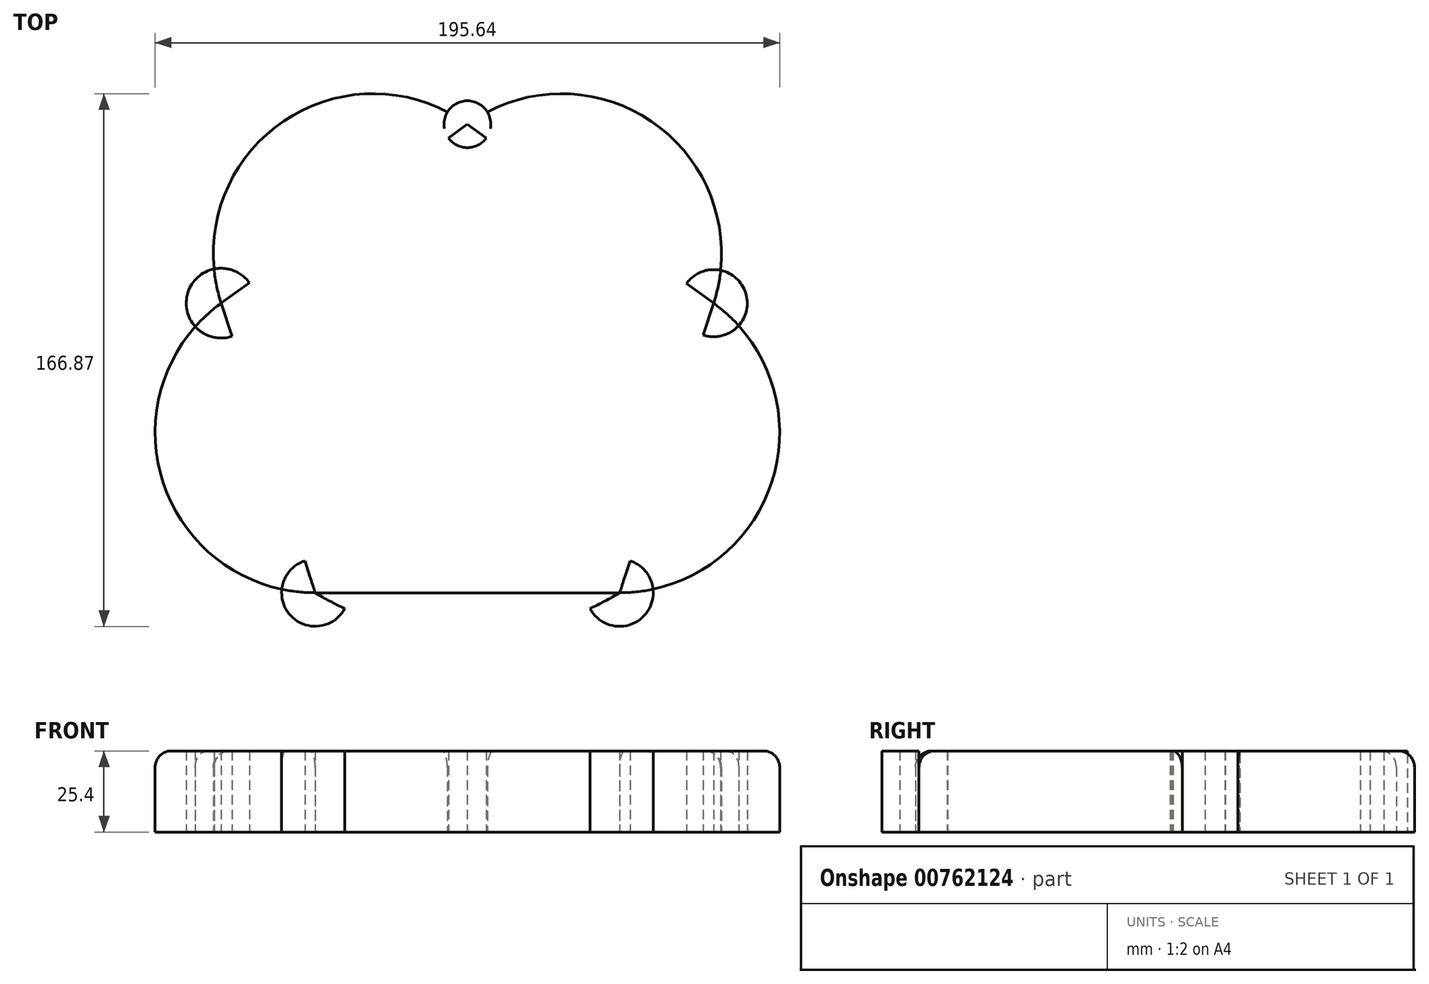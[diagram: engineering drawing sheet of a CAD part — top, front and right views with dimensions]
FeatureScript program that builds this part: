
annotation { "Feature Type Name" : "Feature", "Feature Type Description" : "" }
export const myFeature = defineFeature(function(context is Context, id is Id, definition is map)
    precondition{}
    {
        {
            var Q0;
            Q0=qCreatedBy(makeId("Top.planeOp"),FACE);
            var sketch = newSketch(context, id + "F0", { "sketchPlane" : qUnion([Q0])});
            skCircle(sketch, "E0.cCircle", {"center": v(0, 0) * mm, "radius": 65.63 * mm, "construction": true});
            skLineSegment(sketch, "E0.0", {"start": v(47.68, -65.63) * mm, "end": v(-47.68, -65.63) * mm});
            skLineSegment(sketch, "E0.1", {"start": v(-47.68, -65.63) * mm, "end": v(-77.15, 25.07) * mm});
            skLineSegment(sketch, "E0.2", {"start": v(-77.15, 25.07) * mm, "end": v(0, 81.12) * mm});
            skLineSegment(sketch, "E0.3", {"start": v(0, 81.12) * mm, "end": v(77.15, 25.07) * mm});
            skLineSegment(sketch, "E0.4", {"start": v(77.15, 25.07) * mm, "end": v(47.68, -65.63) * mm});
            skPoint(sketch, "E0.0.midPoint", {"position": v(0, -65.63) * mm});
            skCircle(sketch, "E1", {"center": v(-77.15, 25.07) * mm, "radius": 10.93 * mm});
            skCircle(sketch, "E2", {"center": v(0, 81.12) * mm, "radius": 7.34 * mm});
            skCircle(sketch, "E3", {"center": v(77.15, 25.07) * mm, "radius": 10.52 * mm});
            skCircle(sketch, "E4", {"center": v(47.68, -65.63) * mm, "radius": 10.54 * mm});
            skCircle(sketch, "E5", {"center": v(-47.68, -65.63) * mm, "radius": 10.5 * mm});
            skArc(sketch, "E6", {"start": v(-77.15, 25.07) * mm, "mid": v(-95.37, -30.99) * mm, "end": v(-47.68, -65.63) * mm});
            skArc(sketch, "E7", {"start": v(0, 81.12) * mm, "mid": v(-58.94, 81.12) * mm, "end": v(-77.15, 25.07) * mm});
            skArc(sketch, "E8", {"start": v(77.15, 25.07) * mm, "mid": v(58.94, 81.12) * mm, "end": v(0, 81.12) * mm});
            skArc(sketch, "E9", {"start": v(47.68, -65.63) * mm, "mid": v(95.37, -30.99) * mm, "end": v(77.15, 25.07) * mm});
            skArc(sketch, "E10", {"start": v(-47.68, -65.63) * mm, "mid": v(0, -79.02) * mm, "end": v(47.68, -65.63) * mm});
            skSolve(sketch);
        }
        {
            var Q0;
            {var subQ0=sQuery(id+"F0.wireOp",EDGE,"E7");var subQ1=sQuery(id+"F0.wireOp",EDGE,"E2");var subQ2=makeQuery(id+"F0.imprint","INTERSECT",VERTEX,{"derivedFrom":[subQ1,subQ0]});Q0=makeQuery(id+"F0.imprint","IMPRINT",FACE,{"disambiguationData":[TD([[makeQuery(id+"F0.imprint","IMPRINT",EDGE,{"disambiguationData":[TD([[subQ2,1.0]])],"derivedFrom":subQ1}),1.0]])]});}
            var Q1;
            {var subQ0=sQuery(id+"F0.wireOp",EDGE,"E8");var subQ1=sQuery(id+"F0.wireOp",EDGE,"E3");var subQ2=makeQuery(id+"F0.imprint","INTERSECT",VERTEX,{"derivedFrom":[subQ1,subQ0]});Q1=makeQuery(id+"F0.imprint","IMPRINT",FACE,{"disambiguationData":[TD([[makeQuery(id+"F0.imprint","IMPRINT",EDGE,{"disambiguationData":[TD([[subQ2,1.0]])],"derivedFrom":subQ1}),1.0]])]});}
            var Q2;
            {var subQ0=sQuery(id+"F0.wireOp",EDGE,"E9");var subQ1=sQuery(id+"F0.wireOp",EDGE,"E4");var subQ2=makeQuery(id+"F0.imprint","INTERSECT",VERTEX,{"derivedFrom":[subQ1,subQ0]});Q2=makeQuery(id+"F0.imprint","IMPRINT",FACE,{"disambiguationData":[TD([[makeQuery(id+"F0.imprint","IMPRINT",EDGE,{"disambiguationData":[TD([[subQ2,1.0]])],"derivedFrom":subQ1}),1.0]])]});}
            var Q3;
            {var subQ0=sQuery(id+"F0.wireOp",EDGE,"E6");var subQ1=sQuery(id+"F0.wireOp",EDGE,"E5");var subQ2=makeQuery(id+"F0.imprint","INTERSECT",VERTEX,{"derivedFrom":[subQ1,subQ0]});Q3=makeQuery(id+"F0.imprint","IMPRINT",FACE,{"disambiguationData":[TD([[makeQuery(id+"F0.imprint","IMPRINT",EDGE,{"disambiguationData":[TD([[subQ2,-1.0]])],"derivedFrom":subQ1}),1.0]])]});}
            var Q4;
            {var subQ0=sQuery(id+"F0.wireOp",EDGE,"E5");var subQ1=sQuery(id+"F0.wireOp",EDGE,"E0.1");var subQ2=makeQuery(id+"F0.imprint","INTERSECT",VERTEX,{"derivedFrom":[subQ1,subQ0]});Q4=makeQuery(id+"F0.imprint","IMPRINT",FACE,{"disambiguationData":[TD([[makeQuery(id+"F0.imprint","IMPRINT",EDGE,{"disambiguationData":[TD([[subQ2,-1.0]])],"derivedFrom":subQ1}),1.0]])]});}
            var Q5;
            {var subQ0=sQuery(id+"F0.wireOp",EDGE,"E1");var subQ1=sQuery(id+"F0.wireOp",EDGE,"E0.2");var subQ2=makeQuery(id+"F0.imprint","INTERSECT",VERTEX,{"derivedFrom":[subQ1,subQ0]});Q5=makeQuery(id+"F0.imprint","IMPRINT",FACE,{"disambiguationData":[TD([[makeQuery(id+"F0.imprint","IMPRINT",EDGE,{"disambiguationData":[TD([[subQ2,-1.0]])],"derivedFrom":subQ1}),1.0]])]});}
            var Q6;
            {var subQ0=sQuery(id+"F0.wireOp",EDGE,"E7");var subQ3=sQuery(id+"F0.wireOp",EDGE,"E2");var subQ5=makeQuery(id+"F0.imprint","INTERSECT",VERTEX,{"derivedFrom":[subQ3,subQ0]});Q6=makeQuery(id+"F0.imprint","IMPRINT",FACE,{"disambiguationData":[TD([[makeQuery(id+"F0.imprint","IMPRINT",EDGE,{"disambiguationData":[TD([[subQ5,-1.0]])],"derivedFrom":subQ3}),1.0]])]});}
            var Q7;
            {var subQ0=sQuery(id+"F0.wireOp",EDGE,"E8");var subQ3=sQuery(id+"F0.wireOp",EDGE,"E2");var subQ5=makeQuery(id+"F0.imprint","INTERSECT",VERTEX,{"derivedFrom":[subQ3,subQ0]});Q7=makeQuery(id+"F0.imprint","IMPRINT",FACE,{"disambiguationData":[TD([[makeQuery(id+"F0.imprint","IMPRINT",EDGE,{"disambiguationData":[TD([[subQ5,1.0]])],"derivedFrom":subQ3}),1.0]])]});}
            var Q8;
            {var subQ0=sQuery(id+"F0.wireOp",EDGE,"E2");var subQ1=sQuery(id+"F0.wireOp",EDGE,"E0.3");var subQ2=makeQuery(id+"F0.imprint","INTERSECT",VERTEX,{"derivedFrom":[subQ1,subQ0]});Q8=makeQuery(id+"F0.imprint","IMPRINT",FACE,{"disambiguationData":[TD([[makeQuery(id+"F0.imprint","IMPRINT",EDGE,{"disambiguationData":[TD([[subQ2,-1.0]])],"derivedFrom":subQ1}),1.0]])]});}
            var Q9;
            {var subQ0=sQuery(id+"F0.wireOp",EDGE,"E3");var subQ1=sQuery(id+"F0.wireOp",EDGE,"E0.4");var subQ2=makeQuery(id+"F0.imprint","INTERSECT",VERTEX,{"derivedFrom":[subQ1,subQ0]});Q9=makeQuery(id+"F0.imprint","IMPRINT",FACE,{"disambiguationData":[TD([[makeQuery(id+"F0.imprint","IMPRINT",EDGE,{"disambiguationData":[TD([[subQ2,-1.0]])],"derivedFrom":subQ1}),1.0]])]});}
            var Q10;
            {var subQ13=sQuery(id+"F0.wireOp",EDGE,"E4");var subQ14=sQuery(id+"F0.wireOp",EDGE,"E0.0");var subQ15=makeQuery(id+"F0.imprint","INTERSECT",VERTEX,{"derivedFrom":[subQ14,subQ13]});Q10=makeQuery(id+"F0.imprint","IMPRINT",FACE,{"disambiguationData":[TD([[makeQuery(id+"F0.imprint","IMPRINT",EDGE,{"disambiguationData":[TD([[subQ15,-1.0]])],"derivedFrom":subQ14}),-1.0]])]});}
            var Q11;
            {var subQ0=sQuery(id+"F0.wireOp",EDGE,"E7");var subQ1=sQuery(id+"F0.wireOp",EDGE,"E1");var subQ2=makeQuery(id+"F0.imprint","INTERSECT",VERTEX,{"derivedFrom":[subQ1,subQ0]});Q11=makeQuery(id+"F0.imprint","IMPRINT",FACE,{"disambiguationData":[TD([[makeQuery(id+"F0.imprint","IMPRINT",EDGE,{"disambiguationData":[TD([[subQ2,-1.0]])],"derivedFrom":subQ1}),1.0]])]});}
            var Q12;
            {var subQ1=sQuery(id+"F0.wireOp",EDGE,"E0.3");var subQ3=sQuery(id+"F0.wireOp",EDGE,"E3");var subQ4=makeQuery(id+"F0.imprint","INTERSECT",VERTEX,{"derivedFrom":[subQ1,subQ3]});Q12=makeQuery(id+"F0.imprint","IMPRINT",FACE,{"disambiguationData":[TD([[makeQuery(id+"F0.imprint","IMPRINT",EDGE,{"disambiguationData":[TD([[subQ4,-1.0]])],"derivedFrom":subQ3}),1.0]])]});}
            var Q13;
            {var subQ1=sQuery(id+"F0.wireOp",EDGE,"E0.1");var subQ3=sQuery(id+"F0.wireOp",EDGE,"E1");var subQ4=makeQuery(id+"F0.imprint","INTERSECT",VERTEX,{"derivedFrom":[subQ1,subQ3]});Q13=makeQuery(id+"F0.imprint","IMPRINT",FACE,{"disambiguationData":[TD([[makeQuery(id+"F0.imprint","IMPRINT",EDGE,{"disambiguationData":[TD([[subQ4,-1.0]])],"derivedFrom":subQ3}),1.0]])]});}
            var Q14;
            {var subQ1=sQuery(id+"F0.wireOp",EDGE,"E0.0");var subQ3=sQuery(id+"F0.wireOp",EDGE,"E4");var subQ4=makeQuery(id+"F0.imprint","INTERSECT",VERTEX,{"derivedFrom":[subQ1,subQ3]});Q14=makeQuery(id+"F0.imprint","IMPRINT",FACE,{"disambiguationData":[TD([[makeQuery(id+"F0.imprint","IMPRINT",EDGE,{"disambiguationData":[TD([[subQ4,1.0]])],"derivedFrom":subQ3}),1.0]])]});}
            var Q15;
            {var subQ1=sQuery(id+"F0.wireOp",EDGE,"E0.0");var subQ3=sQuery(id+"F0.wireOp",EDGE,"E5");var subQ4=makeQuery(id+"F0.imprint","INTERSECT",VERTEX,{"derivedFrom":[subQ1,subQ3]});Q15=makeQuery(id+"F0.imprint","IMPRINT",FACE,{"disambiguationData":[TD([[makeQuery(id+"F0.imprint","IMPRINT",EDGE,{"disambiguationData":[TD([[subQ4,-1.0]])],"derivedFrom":subQ3}),1.0]])]});}
            extrude(context, id + "F1", {"entities" : qUnion([Q0, Q1, Q2, Q3, Q4, Q5, Q6, Q7, Q8, Q9, Q10, Q11, Q12, Q13, Q14, Q15]), "depth" : 25.4 * mm, "offsetDistance" : 25.4 * mm});
        }
        {
            var Q0;
            {var subQ0=sQuery(id+"F0.wireOp",EDGE,"E8");Q0=makeQuery(id+"F1.opExtrude","CAP_EDGE",EDGE,{"disambiguationData":[OSD([subQ0]),TDD([makeQuery(id+"F0.imprint","IMPRINT",EDGE,{"disambiguationData":[TD([[makeQuery(id+"F0.imprint","INTERSECT",VERTEX,{"derivedFrom":[sQuery(id+"F0.wireOp",EDGE,"E2"),subQ0]}),1.0]])],"derivedFrom":subQ0})])],"isStart":false});}
            var Q1;
            {var subQ0=sQuery(id+"F0.wireOp",EDGE,"E9");Q1=makeQuery(id+"F1.opExtrude","CAP_EDGE",EDGE,{"disambiguationData":[OSD([subQ0]),TDD([makeQuery(id+"F0.imprint","IMPRINT",EDGE,{"disambiguationData":[TD([[makeQuery(id+"F0.imprint","INTERSECT",VERTEX,{"derivedFrom":[sQuery(id+"F0.wireOp",EDGE,"E3"),subQ0]}),1.0]])],"derivedFrom":subQ0})])],"isStart":false});}
            var Q2;
            Q2=makeQuery(id+"F1.opExtrude","CAP_EDGE",EDGE,{"disambiguationData":[OSD([sQuery(id+"F0.wireOp",EDGE,"E0.0")])],"isStart":false});
            var Q3;
            {var subQ0=sQuery(id+"F0.wireOp",EDGE,"E6");Q3=makeQuery(id+"F1.opExtrude","CAP_EDGE",EDGE,{"disambiguationData":[OSD([subQ0]),TDD([makeQuery(id+"F0.imprint","IMPRINT",EDGE,{"disambiguationData":[TD([[makeQuery(id+"F0.imprint","INTERSECT",VERTEX,{"derivedFrom":[sQuery(id+"F0.wireOp",EDGE,"E1"),subQ0]}),-1.0]])],"derivedFrom":subQ0})])],"isStart":false});}
            var Q4;
            {var subQ0=sQuery(id+"F0.wireOp",EDGE,"E7");Q4=makeQuery(id+"F1.opExtrude","CAP_EDGE",EDGE,{"disambiguationData":[OSD([subQ0]),TDD([makeQuery(id+"F0.imprint","IMPRINT",EDGE,{"disambiguationData":[TD([[makeQuery(id+"F0.imprint","INTERSECT",VERTEX,{"derivedFrom":[sQuery(id+"F0.wireOp",EDGE,"E1"),subQ0]}),1.0]])],"derivedFrom":subQ0})])],"isStart":false});}
            fillet(context, id + "F2", {"entities" : qUnion([Q0, Q1, Q2, Q3, Q4]), "radius" : 5.08 * mm, "tangentPropagation" : true, "allowEdgeOverflow" : false});
        }
    });
